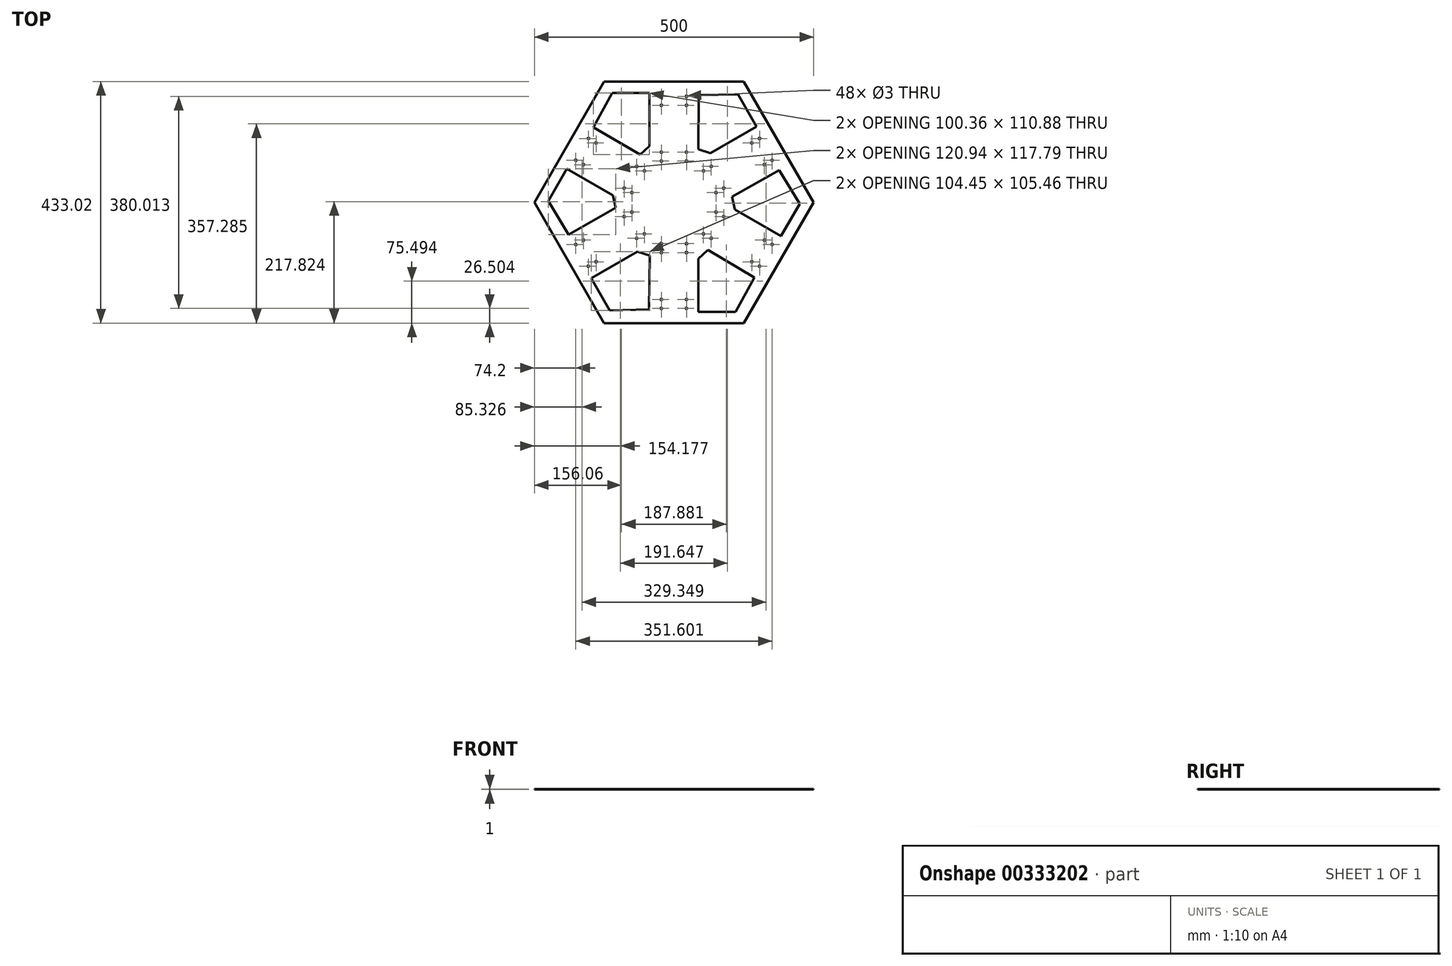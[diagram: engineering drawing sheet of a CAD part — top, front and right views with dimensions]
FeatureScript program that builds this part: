
annotation { "Feature Type Name" : "Feature", "Feature Type Description" : "" }
export const myFeature = defineFeature(function(context is Context, id is Id, definition is map)
    precondition{}
    {
        {
            var Q0;
            Q0=qCreatedBy(makeId("Top.planeOp"),FACE);
            var sketch = newSketch(context, id + "F0", { "sketchPlane" : qUnion([Q0])});
            skCircle(sketch, "E0.cCircle", {"center": v(0, 0) * mm, "radius": 250 * mm, "construction": true});
            skLineSegment(sketch, "E0.0", {"start": v(250, 0) * mm, "end": v(125, -216.5) * mm});
            skLineSegment(sketch, "E0.1", {"start": v(125, -216.5) * mm, "end": v(-125, -216.5) * mm});
            skLineSegment(sketch, "E0.2", {"start": v(-125, -216.5) * mm, "end": v(-250, 0) * mm});
            skLineSegment(sketch, "E0.3", {"start": v(-250, 0) * mm, "end": v(-125, 216.5) * mm});
            skLineSegment(sketch, "E0.4", {"start": v(-125, 216.5) * mm, "end": v(125, 216.5) * mm});
            skLineSegment(sketch, "E0.5", {"start": v(125, 216.5) * mm, "end": v(250, 0) * mm});
            skCircle(sketch, "E1", {"center": v(-22.5, 190) * mm, "radius": 1.5 * mm});
            skCircle(sketch, "E2.MirrorC", {"center": v(22.5, 190) * mm, "radius": 1.5 * mm});
            skCircle(sketch, "E3.0.1.0", {"center": v(-22.5, 174) * mm, "radius": 1.5 * mm});
            skCircle(sketch, "E3.0.1.1", {"center": v(22.5, 174) * mm, "radius": 1.5 * mm});
            skLineSegment(sketch, "E3.direction1", {"start": v(-22.5, 190) * mm, "end": v(2.5, 190) * mm, "construction": true});
            skLineSegment(sketch, "E3.direction2", {"start": v(-22.5, 190) * mm, "end": v(-22.5, 174) * mm, "construction": true});
            skCircle(sketch, "E4.0.1.0", {"center": v(22.5, 90) * mm, "radius": 1.5 * mm});
            skCircle(sketch, "E4.0.1.1", {"center": v(-22.5, 74) * mm, "radius": 1.5 * mm});
            skCircle(sketch, "E4.0.1.2", {"center": v(22.5, 74) * mm, "radius": 1.5 * mm});
            skLineSegment(sketch, "E4.0.1.3", {"start": v(-22.5, 90) * mm, "end": v(2.5, 90) * mm, "construction": true});
            skLineSegment(sketch, "E4.0.1.4", {"start": v(-22.5, 90) * mm, "end": v(-22.5, 74) * mm, "construction": true});
            skCircle(sketch, "E4.0.1.5", {"center": v(-22.5, 90) * mm, "radius": 1.5 * mm});
            skLineSegment(sketch, "E4.direction1", {"start": v(-22.5, 174) * mm, "end": v(2.5, 174) * mm, "construction": true});
            skLineSegment(sketch, "E4.direction2", {"start": v(-22.5, 174) * mm, "end": v(-22.5, 74) * mm, "construction": true});
            skLineSegment(sketch, "E5.1.0", {"start": v(-175.8, 75.52) * mm, "end": v(-163.3, 97.17) * mm, "construction": true});
            skLineSegment(sketch, "E5.1.1", {"start": v(-175.8, 75.52) * mm, "end": v(-161.94, 67.52) * mm, "construction": true});
            skLineSegment(sketch, "E5.1.2", {"start": v(-161.94, 67.52) * mm, "end": v(-75.34, 17.52) * mm, "construction": true});
            skLineSegment(sketch, "E5.1.3", {"start": v(-89.2, 25.52) * mm, "end": v(-76.7, 47.17) * mm, "construction": true});
            skLineSegment(sketch, "E5.1.4", {"start": v(-161.94, 67.52) * mm, "end": v(-149.44, 89.17) * mm, "construction": true});
            skCircle(sketch, "E5.1.5", {"center": v(-66.7, 64.49) * mm, "radius": 1.5 * mm});
            skLineSegment(sketch, "E5.1.6", {"start": v(-89.2, 25.52) * mm, "end": v(-75.34, 17.52) * mm, "construction": true});
            skCircle(sketch, "E5.1.7", {"center": v(-52.84, 56.49) * mm, "radius": 1.5 * mm});
            skCircle(sketch, "E5.1.8", {"center": v(-153.3, 114.49) * mm, "radius": 1.5 * mm});
            skCircle(sketch, "E5.1.9", {"center": v(-139.44, 106.49) * mm, "radius": 1.5 * mm});
            skCircle(sketch, "E5.1.10", {"center": v(-75.34, 17.52) * mm, "radius": 1.5 * mm});
            skCircle(sketch, "E5.1.11", {"center": v(-175.8, 75.52) * mm, "radius": 1.5 * mm});
            skCircle(sketch, "E5.1.12", {"center": v(-89.2, 25.52) * mm, "radius": 1.5 * mm});
            skCircle(sketch, "E5.1.13", {"center": v(-161.94, 67.52) * mm, "radius": 1.5 * mm});
            skLineSegment(sketch, "E5.2.0", {"start": v(-153.3, -114.49) * mm, "end": v(-165.8, -92.84) * mm, "construction": true});
            skLineSegment(sketch, "E5.2.1", {"start": v(-153.3, -114.49) * mm, "end": v(-139.44, -106.49) * mm, "construction": true});
            skLineSegment(sketch, "E5.2.2", {"start": v(-139.44, -106.49) * mm, "end": v(-52.84, -56.49) * mm, "construction": true});
            skLineSegment(sketch, "E5.2.3", {"start": v(-66.7, -64.49) * mm, "end": v(-79.2, -42.84) * mm, "construction": true});
            skLineSegment(sketch, "E5.2.4", {"start": v(-139.44, -106.49) * mm, "end": v(-151.94, -84.84) * mm, "construction": true});
            skCircle(sketch, "E5.2.5", {"center": v(-89.2, -25.52) * mm, "radius": 1.5 * mm});
            skLineSegment(sketch, "E5.2.6", {"start": v(-66.7, -64.49) * mm, "end": v(-52.84, -56.49) * mm, "construction": true});
            skCircle(sketch, "E5.2.7", {"center": v(-75.34, -17.52) * mm, "radius": 1.5 * mm});
            skCircle(sketch, "E5.2.8", {"center": v(-175.8, -75.52) * mm, "radius": 1.5 * mm});
            skCircle(sketch, "E5.2.9", {"center": v(-161.94, -67.52) * mm, "radius": 1.5 * mm});
            skCircle(sketch, "E5.2.10", {"center": v(-52.84, -56.49) * mm, "radius": 1.5 * mm});
            skCircle(sketch, "E5.2.11", {"center": v(-153.3, -114.49) * mm, "radius": 1.5 * mm});
            skCircle(sketch, "E5.2.12", {"center": v(-66.7, -64.49) * mm, "radius": 1.5 * mm});
            skCircle(sketch, "E5.2.13", {"center": v(-139.44, -106.49) * mm, "radius": 1.5 * mm});
            skLineSegment(sketch, "E5.3.0", {"start": v(22.5, -190) * mm, "end": v(-2.5, -190) * mm, "construction": true});
            skLineSegment(sketch, "E5.3.1", {"start": v(22.5, -190) * mm, "end": v(22.5, -174) * mm, "construction": true});
            skLineSegment(sketch, "E5.3.2", {"start": v(22.5, -174) * mm, "end": v(22.5, -74) * mm, "construction": true});
            skLineSegment(sketch, "E5.3.3", {"start": v(22.5, -90) * mm, "end": v(-2.5, -90) * mm, "construction": true});
            skLineSegment(sketch, "E5.3.4", {"start": v(22.5, -174) * mm, "end": v(-2.5, -174) * mm, "construction": true});
            skCircle(sketch, "E5.3.5", {"center": v(-22.5, -90) * mm, "radius": 1.5 * mm});
            skLineSegment(sketch, "E5.3.6", {"start": v(22.5, -90) * mm, "end": v(22.5, -74) * mm, "construction": true});
            skCircle(sketch, "E5.3.7", {"center": v(-22.5, -74) * mm, "radius": 1.5 * mm});
            skCircle(sketch, "E5.3.8", {"center": v(-22.5, -190) * mm, "radius": 1.5 * mm});
            skCircle(sketch, "E5.3.9", {"center": v(-22.5, -174) * mm, "radius": 1.5 * mm});
            skCircle(sketch, "E5.3.10", {"center": v(22.5, -74) * mm, "radius": 1.5 * mm});
            skCircle(sketch, "E5.3.11", {"center": v(22.5, -190) * mm, "radius": 1.5 * mm});
            skCircle(sketch, "E5.3.12", {"center": v(22.5, -90) * mm, "radius": 1.5 * mm});
            skCircle(sketch, "E5.3.13", {"center": v(22.5, -174) * mm, "radius": 1.5 * mm});
            skLineSegment(sketch, "E5.4.0", {"start": v(175.8, -75.52) * mm, "end": v(163.3, -97.17) * mm, "construction": true});
            skLineSegment(sketch, "E5.4.1", {"start": v(175.8, -75.52) * mm, "end": v(161.94, -67.52) * mm, "construction": true});
            skLineSegment(sketch, "E5.4.2", {"start": v(161.94, -67.52) * mm, "end": v(75.34, -17.52) * mm, "construction": true});
            skLineSegment(sketch, "E5.4.3", {"start": v(89.2, -25.52) * mm, "end": v(76.7, -47.17) * mm, "construction": true});
            skLineSegment(sketch, "E5.4.4", {"start": v(161.94, -67.52) * mm, "end": v(149.44, -89.17) * mm, "construction": true});
            skCircle(sketch, "E5.4.5", {"center": v(66.7, -64.49) * mm, "radius": 1.5 * mm});
            skLineSegment(sketch, "E5.4.6", {"start": v(89.2, -25.52) * mm, "end": v(75.34, -17.52) * mm, "construction": true});
            skCircle(sketch, "E5.4.7", {"center": v(52.84, -56.49) * mm, "radius": 1.5 * mm});
            skCircle(sketch, "E5.4.8", {"center": v(153.3, -114.49) * mm, "radius": 1.5 * mm});
            skCircle(sketch, "E5.4.9", {"center": v(139.44, -106.49) * mm, "radius": 1.5 * mm});
            skCircle(sketch, "E5.4.10", {"center": v(75.34, -17.52) * mm, "radius": 1.5 * mm});
            skCircle(sketch, "E5.4.11", {"center": v(175.8, -75.52) * mm, "radius": 1.5 * mm});
            skCircle(sketch, "E5.4.12", {"center": v(89.2, -25.52) * mm, "radius": 1.5 * mm});
            skCircle(sketch, "E5.4.13", {"center": v(161.94, -67.52) * mm, "radius": 1.5 * mm});
            skLineSegment(sketch, "E5.5.0", {"start": v(153.3, 114.49) * mm, "end": v(165.8, 92.84) * mm, "construction": true});
            skLineSegment(sketch, "E5.5.1", {"start": v(153.3, 114.49) * mm, "end": v(139.44, 106.49) * mm, "construction": true});
            skLineSegment(sketch, "E5.5.2", {"start": v(139.44, 106.49) * mm, "end": v(52.84, 56.49) * mm, "construction": true});
            skLineSegment(sketch, "E5.5.3", {"start": v(66.7, 64.49) * mm, "end": v(79.2, 42.84) * mm, "construction": true});
            skLineSegment(sketch, "E5.5.4", {"start": v(139.44, 106.49) * mm, "end": v(151.94, 84.84) * mm, "construction": true});
            skCircle(sketch, "E5.5.5", {"center": v(89.2, 25.52) * mm, "radius": 1.5 * mm});
            skLineSegment(sketch, "E5.5.6", {"start": v(66.7, 64.49) * mm, "end": v(52.84, 56.49) * mm, "construction": true});
            skCircle(sketch, "E5.5.7", {"center": v(75.34, 17.52) * mm, "radius": 1.5 * mm});
            skCircle(sketch, "E5.5.8", {"center": v(175.8, 75.52) * mm, "radius": 1.5 * mm});
            skCircle(sketch, "E5.5.9", {"center": v(161.94, 67.52) * mm, "radius": 1.5 * mm});
            skCircle(sketch, "E5.5.10", {"center": v(52.84, 56.49) * mm, "radius": 1.5 * mm});
            skCircle(sketch, "E5.5.11", {"center": v(153.3, 114.49) * mm, "radius": 1.5 * mm});
            skCircle(sketch, "E5.5.12", {"center": v(66.7, 64.49) * mm, "radius": 1.5 * mm});
            skCircle(sketch, "E5.5.13", {"center": v(139.44, 106.49) * mm, "radius": 1.5 * mm});
            skSolve(sketch);
        }
        {
            var Q0;
            Q0=makeQuery(id+"F0.imprint","IMPRINT",FACE,{"disambiguationData":[TD([[makeQuery(id+"F0.imprint","IMPRINT",EDGE,{"derivedFrom":sQuery(id+"F0.wireOp",EDGE,"E0.0")}),-1.0]])]});
            extrude(context, id + "F1", {"entities" : qUnion([Q0]), "depth" : 1 * mm});
        }
        {
            var Q0;
            Q0=makeQuery(id+"F1.opExtrude","CAP_FACE",FACE,{"disambiguationData":[OSD([sQuery(id+"F0.wireOp",EDGE,"E0.0"),sQuery(id+"F0.wireOp",EDGE,"E0.1"),sQuery(id+"F0.wireOp",EDGE,"E0.2"),sQuery(id+"F0.wireOp",EDGE,"E0.3"),sQuery(id+"F0.wireOp",EDGE,"E0.4"),sQuery(id+"F0.wireOp",EDGE,"E0.5"),sQuery(id+"F0.wireOp",EDGE,"E1"),sQuery(id+"F0.wireOp",EDGE,"E2.MirrorC"),sQuery(id+"F0.wireOp",EDGE,"E3.0.1.0"),sQuery(id+"F0.wireOp",EDGE,"E3.0.1.1"),sQuery(id+"F0.wireOp",EDGE,"E4.0.1.0"),sQuery(id+"F0.wireOp",EDGE,"E4.0.1.1"),sQuery(id+"F0.wireOp",EDGE,"E4.0.1.2"),sQuery(id+"F0.wireOp",EDGE,"E4.0.1.5"),sQuery(id+"F0.wireOp",EDGE,"E5.1.5"),sQuery(id+"F0.wireOp",EDGE,"E5.1.7"),sQuery(id+"F0.wireOp",EDGE,"E5.1.8"),sQuery(id+"F0.wireOp",EDGE,"E5.1.9"),sQuery(id+"F0.wireOp",EDGE,"E5.1.10"),sQuery(id+"F0.wireOp",EDGE,"E5.1.11"),sQuery(id+"F0.wireOp",EDGE,"E5.1.12"),sQuery(id+"F0.wireOp",EDGE,"E5.1.13"),sQuery(id+"F0.wireOp",EDGE,"E5.2.5"),sQuery(id+"F0.wireOp",EDGE,"E5.2.7"),sQuery(id+"F0.wireOp",EDGE,"E5.2.8"),sQuery(id+"F0.wireOp",EDGE,"E5.2.9"),sQuery(id+"F0.wireOp",EDGE,"E5.2.10"),sQuery(id+"F0.wireOp",EDGE,"E5.2.11"),sQuery(id+"F0.wireOp",EDGE,"E5.2.12"),sQuery(id+"F0.wireOp",EDGE,"E5.2.13"),sQuery(id+"F0.wireOp",EDGE,"E5.3.5"),sQuery(id+"F0.wireOp",EDGE,"E5.3.7"),sQuery(id+"F0.wireOp",EDGE,"E5.3.8"),sQuery(id+"F0.wireOp",EDGE,"E5.3.9"),sQuery(id+"F0.wireOp",EDGE,"E5.3.10"),sQuery(id+"F0.wireOp",EDGE,"E5.3.11"),sQuery(id+"F0.wireOp",EDGE,"E5.3.12"),sQuery(id+"F0.wireOp",EDGE,"E5.3.13"),sQuery(id+"F0.wireOp",EDGE,"E5.4.5"),sQuery(id+"F0.wireOp",EDGE,"E5.4.7"),sQuery(id+"F0.wireOp",EDGE,"E5.4.8"),sQuery(id+"F0.wireOp",EDGE,"E5.4.9"),sQuery(id+"F0.wireOp",EDGE,"E5.4.10"),sQuery(id+"F0.wireOp",EDGE,"E5.4.11"),sQuery(id+"F0.wireOp",EDGE,"E5.4.12"),sQuery(id+"F0.wireOp",EDGE,"E5.4.13"),sQuery(id+"F0.wireOp",EDGE,"E5.5.5"),sQuery(id+"F0.wireOp",EDGE,"E5.5.7"),sQuery(id+"F0.wireOp",EDGE,"E5.5.8"),sQuery(id+"F0.wireOp",EDGE,"E5.5.9"),sQuery(id+"F0.wireOp",EDGE,"E5.5.10"),sQuery(id+"F0.wireOp",EDGE,"E5.5.11"),sQuery(id+"F0.wireOp",EDGE,"E5.5.12"),sQuery(id+"F0.wireOp",EDGE,"E5.5.13")])],"isStart":false});
            var sketch = newSketch(context, id + "F2", { "sketchPlane" : qUnion([Q0])});
            skLineSegment(sketch, "E6", {"start": v(-144.12, 134.46) * mm, "end": v(-110.43, 196.22) * mm});
            skLineSegment(sketch, "E7", {"start": v(-110.43, 196.22) * mm, "end": v(-43.76, 196.22) * mm});
            skLineSegment(sketch, "E8", {"start": v(-43.76, 196.22) * mm, "end": v(-43.76, 100.77) * mm});
            skLineSegment(sketch, "E9", {"start": v(-43.76, 100.77) * mm, "end": v(-60.6, 85.33) * mm});
            skLineSegment(sketch, "E10", {"start": v(-60.6, 85.33) * mm, "end": v(-144.12, 134.46) * mm});
            skLineSegment(sketch, "E11.1.0", {"start": v(-188.5, -57.58) * mm, "end": v(-225.15, 2.47) * mm});
            skLineSegment(sketch, "E11.1.1", {"start": v(-225.15, 2.47) * mm, "end": v(-191.81, 60.2) * mm});
            skLineSegment(sketch, "E11.1.2", {"start": v(-191.81, 60.2) * mm, "end": v(-109.15, 12.49) * mm});
            skLineSegment(sketch, "E11.1.3", {"start": v(-104.2, -9.82) * mm, "end": v(-188.5, -57.58) * mm});
            skLineSegment(sketch, "E11.1.4", {"start": v(-109.15, 12.49) * mm, "end": v(-104.2, -9.82) * mm});
            skLineSegment(sketch, "E11.2.0", {"start": v(-44.39, -192.04) * mm, "end": v(-114.71, -193.75) * mm});
            skLineSegment(sketch, "E11.2.1", {"start": v(-114.71, -193.75) * mm, "end": v(-148.05, -136) * mm});
            skLineSegment(sketch, "E11.2.2", {"start": v(-148.05, -136) * mm, "end": v(-65.4, -88.29) * mm});
            skLineSegment(sketch, "E11.2.3", {"start": v(-43.6, -95.15) * mm, "end": v(-44.39, -192.04) * mm});
            skLineSegment(sketch, "E11.2.4", {"start": v(-65.4, -88.29) * mm, "end": v(-43.6, -95.15) * mm});
            skLineSegment(sketch, "E11.3.0", {"start": v(144.12, -134.46) * mm, "end": v(110.43, -196.22) * mm});
            skLineSegment(sketch, "E11.3.1", {"start": v(110.43, -196.22) * mm, "end": v(43.76, -196.22) * mm});
            skLineSegment(sketch, "E11.3.2", {"start": v(43.76, -196.22) * mm, "end": v(43.76, -100.77) * mm});
            skLineSegment(sketch, "E11.3.3", {"start": v(60.6, -85.33) * mm, "end": v(144.12, -134.46) * mm});
            skLineSegment(sketch, "E11.3.4", {"start": v(43.76, -100.77) * mm, "end": v(60.6, -85.33) * mm});
            skLineSegment(sketch, "E11.4.0", {"start": v(188.5, 57.58) * mm, "end": v(225.15, -2.47) * mm});
            skLineSegment(sketch, "E11.4.1", {"start": v(225.15, -2.47) * mm, "end": v(191.81, -60.2) * mm});
            skLineSegment(sketch, "E11.4.2", {"start": v(191.81, -60.2) * mm, "end": v(109.15, -12.49) * mm});
            skLineSegment(sketch, "E11.4.3", {"start": v(104.2, 9.82) * mm, "end": v(188.5, 57.58) * mm});
            skLineSegment(sketch, "E11.4.4", {"start": v(109.15, -12.49) * mm, "end": v(104.2, 9.82) * mm});
            skLineSegment(sketch, "E11.5.0", {"start": v(44.39, 192.04) * mm, "end": v(114.71, 193.75) * mm});
            skLineSegment(sketch, "E11.5.1", {"start": v(114.71, 193.75) * mm, "end": v(148.05, 136) * mm});
            skLineSegment(sketch, "E11.5.2", {"start": v(148.05, 136) * mm, "end": v(65.4, 88.29) * mm});
            skLineSegment(sketch, "E11.5.3", {"start": v(43.6, 95.15) * mm, "end": v(44.39, 192.04) * mm});
            skLineSegment(sketch, "E11.5.4", {"start": v(65.4, 88.29) * mm, "end": v(43.6, 95.15) * mm});
            skPoint(sketch, "E11.center", {"position": v(0, 0) * mm});
            skSolve(sketch);
        }
        {
            var Q0;
            Q0=qSketchRegion(id+"F2",true);
            extrude(context, id + "F3", {"entities" : qUnion([Q0]), "operationType" : NewBodyOperationType.REMOVE, "oppositeDirection" : true, "depth" : 25 * mm});
        }
    });
